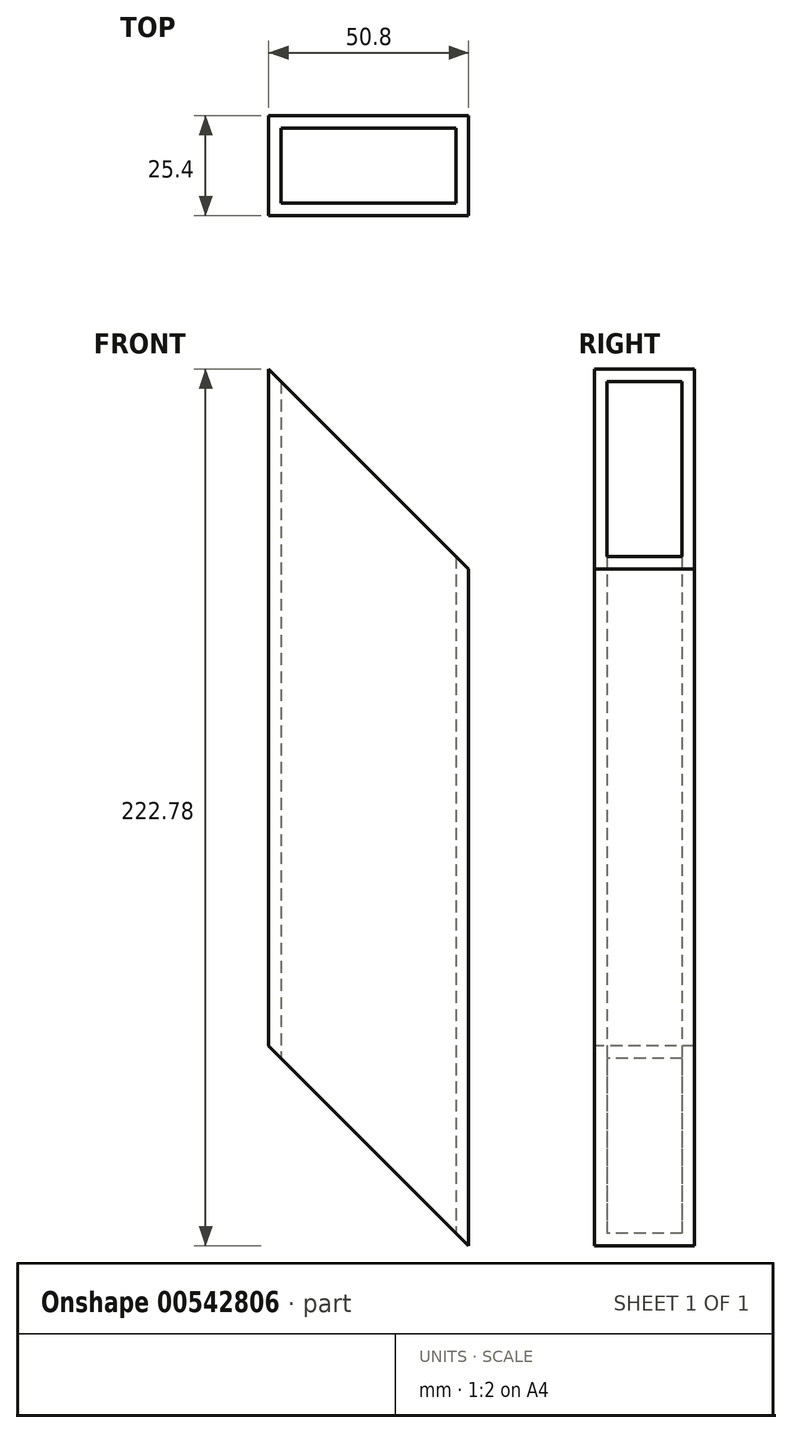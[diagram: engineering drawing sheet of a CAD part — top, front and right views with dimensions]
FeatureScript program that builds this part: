
annotation { "Feature Type Name" : "Feature", "Feature Type Description" : "" }
export const myFeature = defineFeature(function(context is Context, id is Id, definition is map)
    precondition{}
    {
        {
            var Q0;
            Q0=qCreatedBy(makeId("Top.planeOp"),FACE);
            var sketch = newSketch(context, id + "F0", { "sketchPlane" : qUnion([Q0])});
            skLineSegment(sketch, "E0.bottom", {"start": v(-50.8, 25.4) * mm, "end": v(0, 25.4) * mm});
            skLineSegment(sketch, "E0.top", {"start": v(-50.8, 0) * mm, "end": v(0, 0) * mm});
            skLineSegment(sketch, "E0.left", {"start": v(-50.8, 25.4) * mm, "end": v(-50.8, 0) * mm});
            skLineSegment(sketch, "E0.right", {"start": v(0, 25.4) * mm, "end": v(0, 0) * mm});
            skLineSegment(sketch, "E1.bottom", {"start": v(-47.63, 22.23) * mm, "end": v(-3.18, 22.23) * mm});
            skLineSegment(sketch, "E1.top", {"start": v(-47.63, 3.18) * mm, "end": v(-3.18, 3.18) * mm});
            skLineSegment(sketch, "E1.left", {"start": v(-47.63, 22.23) * mm, "end": v(-47.63, 3.18) * mm});
            skLineSegment(sketch, "E1.right", {"start": v(-3.18, 22.23) * mm, "end": v(-3.18, 3.18) * mm});
            skSolve(sketch);
        }
        {
            var Q0;
            Q0=makeQuery(id+"F0.imprint","IMPRINT",FACE,{"disambiguationData":[TD([[makeQuery(id+"F0.imprint","IMPRINT",EDGE,{"derivedFrom":sQuery(id+"F0.wireOp",EDGE,"E0.bottom")}),-1.0]])]});
            extrude(context, id + "F1", {"entities" : qUnion([Q0]), "depth" : 222.78 * mm, "offsetDistance" : 25.4 * mm});
        }
        {
            var Q0;
            Q0=makeQuery(id+"F1.opExtrude","SWEPT_FACE",FACE,{"disambiguationData":[OSD([sQuery(id+"F0.wireOp",EDGE,"E0.top")])]});
            var sketch = newSketch(context, id + "F2", { "sketchPlane" : qUnion([Q0])});
            skLineSegment(sketch, "E2", {"start": v(0, 0) * mm, "end": v(-50.8, 50.8) * mm});
            skLineSegment(sketch, "E3", {"start": v(-50.8, 222.78) * mm, "end": v(0, 171.98) * mm});
            skSolve(sketch);
        }
        {
            var Q0;
            {var subQ0=sQuery(id+"F2.wireOp",EDGE,"E2");Q0=makeQuery(id+"F2.imprint","IMPRINT",FACE,{"disambiguationData":[TD([[makeQuery(id+"F2.imprint","IMPRINT",EDGE,{"derivedFrom":subQ0}),1.0]])]});}
            var Q1;
            {var subQ0=sQuery(id+"F2.wireOp",EDGE,"E3");Q1=makeQuery(id+"F2.imprint","IMPRINT",FACE,{"disambiguationData":[TD([[makeQuery(id+"F2.imprint","IMPRINT",EDGE,{"derivedFrom":subQ0}),1.0]])]});}
            extrude(context, id + "F3", {"entities" : qUnion([Q0, Q1]), "operationType" : NewBodyOperationType.REMOVE, "oppositeDirection" : true, "depth" : 25.4 * mm, "offsetDistance" : 25.4 * mm});
        }
    });
